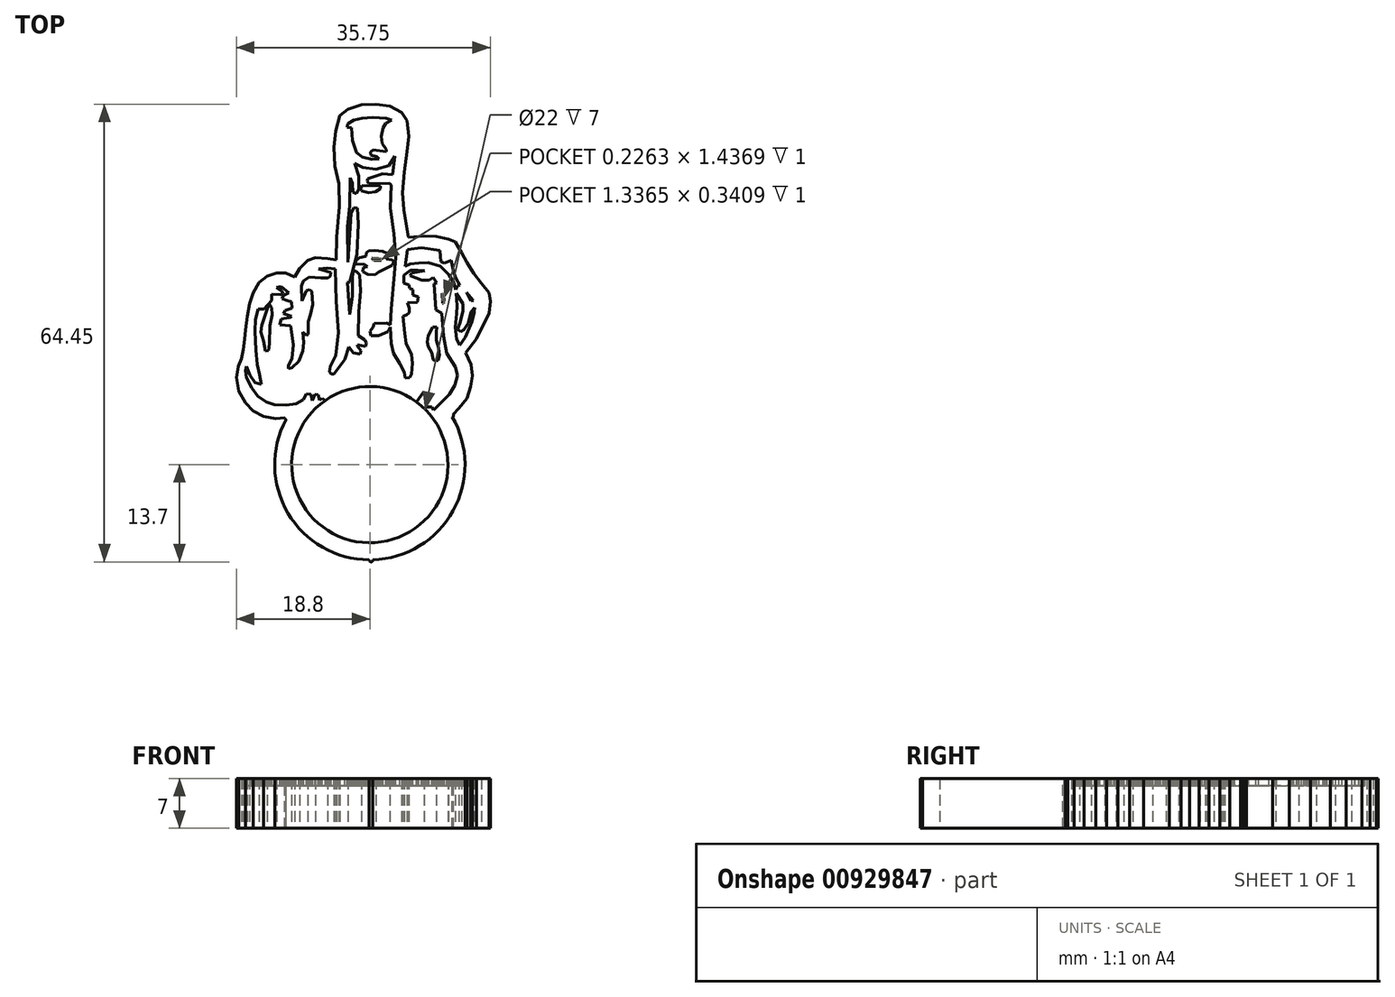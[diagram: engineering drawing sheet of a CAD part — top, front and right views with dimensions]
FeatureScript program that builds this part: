
annotation { "Feature Type Name" : "Feature", "Feature Type Description" : "" }
export const myFeature = defineFeature(function(context is Context, id is Id, definition is map)
    precondition{}
    {
        {
            var Q0;
            Q0=qCreatedBy(makeId("Top.planeOp"),FACE);
            var sketch = newSketch(context, id + "F0", { "sketchPlane" : qUnion([Q0])});
            skCircle(sketch, "E0", {"center": v(0, 0) * mm, "radius": 11 * mm});
            skCircle(sketch, "E1", {"center": v(0, 0) * mm, "radius": 13.4 * mm});
            skCircle(sketch, "E2", {"center": v(0, 0) * mm, "radius": 50.8 * mm, "construction": true});
            skLineSegment(sketch, "E3", {"start": v(0, 0) * mm, "end": v(-44, 25.4) * mm, "construction": true});
            skLineSegment(sketch, "E4", {"start": v(0, 0) * mm, "end": v(44, 25.4) * mm, "construction": true});
            skLineSegment(sketch, "E5", {"start": v(0, 0) * mm, "end": v(0, -50.8) * mm, "construction": true});
            skSolve(sketch);
        }
        {
            var Q0;
            Q0=qCreatedBy(makeId("Top.planeOp"),FACE);
            var sketch = newSketch(context, id + "F1", { "sketchPlane" : qUnion([Q0])});
            skCircle(sketch, "E6.0", {"center": v(0, 0) * mm, "radius": 13.4 * mm});
            skLineSegment(sketch, "E7", {"start": v(-11.66, 6.6) * mm, "end": v(-13.26, 6.5) * mm});
            skLineSegment(sketch, "E8", {"start": v(-13.26, 6.5) * mm, "end": v(-14.97, 6.82) * mm});
            skLineSegment(sketch, "E9", {"start": v(-14.97, 6.82) * mm, "end": v(-16.42, 7.53) * mm});
            skLineSegment(sketch, "E10", {"start": v(-16.42, 7.53) * mm, "end": v(-17.5, 8.7) * mm});
            skLineSegment(sketch, "E11", {"start": v(-17.5, 8.7) * mm, "end": v(-18.45, 10.38) * mm});
            skLineSegment(sketch, "E12", {"start": v(-18.45, 10.38) * mm, "end": v(-18.8, 12.26) * mm});
            skLineSegment(sketch, "E13", {"start": v(-18.8, 12.26) * mm, "end": v(-18.53, 13.84) * mm});
            skLineSegment(sketch, "E14", {"start": v(-18.53, 13.84) * mm, "end": v(-18.08, 14.9) * mm});
            skLineSegment(sketch, "E15", {"start": v(-18.08, 14.9) * mm, "end": v(-17.8, 16.19) * mm});
            skLineSegment(sketch, "E16", {"start": v(-17.8, 16.19) * mm, "end": v(-17.65, 17.63) * mm});
            skLineSegment(sketch, "E17", {"start": v(-17.65, 17.63) * mm, "end": v(-17.47, 19.02) * mm});
            skLineSegment(sketch, "E18", {"start": v(-17.47, 19.02) * mm, "end": v(-17.24, 20.92) * mm});
            skLineSegment(sketch, "E19", {"start": v(-17.24, 20.92) * mm, "end": v(-16.93, 22.67) * mm});
            skLineSegment(sketch, "E20", {"start": v(-16.93, 22.67) * mm, "end": v(-16.4, 24.2) * mm});
            skLineSegment(sketch, "E21", {"start": v(-16.4, 24.2) * mm, "end": v(-15.57, 25.63) * mm});
            skLineSegment(sketch, "E22", {"start": v(-15.57, 25.63) * mm, "end": v(-14.42, 26.52) * mm});
            skLineSegment(sketch, "E23", {"start": v(-14.42, 26.52) * mm, "end": v(-13.13, 26.99) * mm});
            skLineSegment(sketch, "E24", {"start": v(-13.13, 26.99) * mm, "end": v(-11.88, 26.99) * mm});
            skLineSegment(sketch, "E25", {"start": v(-11.88, 26.99) * mm, "end": v(-10.57, 26.44) * mm});
            skLineSegment(sketch, "E26", {"start": v(-10.57, 26.44) * mm, "end": v(-9.87, 27.6) * mm});
            skLineSegment(sketch, "E27", {"start": v(-9.87, 27.6) * mm, "end": v(-8.74, 28.74) * mm});
            skLineSegment(sketch, "E28", {"start": v(-8.74, 28.74) * mm, "end": v(-7.67, 29.15) * mm});
            skLineSegment(sketch, "E29", {"start": v(-7.67, 29.15) * mm, "end": v(-5.97, 29.04) * mm});
            skLineSegment(sketch, "E30", {"start": v(-5.97, 29.04) * mm, "end": v(-4.76, 28.84) * mm});
            skLineSegment(sketch, "E31", {"start": v(-4.76, 28.84) * mm, "end": v(-4.65, 32.06) * mm});
            skLineSegment(sketch, "E32", {"start": v(-4.65, 32.06) * mm, "end": v(-4.28, 36.3) * mm});
            skLineSegment(sketch, "E33", {"start": v(-4.28, 36.3) * mm, "end": v(-4.38, 39.56) * mm});
            skLineSegment(sketch, "E34", {"start": v(-4.38, 39.56) * mm, "end": v(-4.93, 42.06) * mm});
            skLineSegment(sketch, "E35", {"start": v(-4.93, 42.06) * mm, "end": v(-5.07, 44.68) * mm});
            skLineSegment(sketch, "E36", {"start": v(-5.07, 44.68) * mm, "end": v(-4.82, 46.97) * mm});
            skLineSegment(sketch, "E37", {"start": v(-4.82, 46.97) * mm, "end": v(-4.26, 49.12) * mm});
            skLineSegment(sketch, "E38", {"start": v(-4.26, 49.12) * mm, "end": v(-3.1, 50.06) * mm});
            skLineSegment(sketch, "E39", {"start": v(-3.1, 50.06) * mm, "end": v(-1.2, 50.67) * mm});
            skLineSegment(sketch, "E40", {"start": v(-1.2, 50.67) * mm, "end": v(0.84, 50.75) * mm});
            skLineSegment(sketch, "E41", {"start": v(0.84, 50.75) * mm, "end": v(2.84, 50.46) * mm});
            skLineSegment(sketch, "E42", {"start": v(2.84, 50.46) * mm, "end": v(4.45, 49.59) * mm});
            skLineSegment(sketch, "E43", {"start": v(4.45, 49.59) * mm, "end": v(5.24, 48.46) * mm});
            skLineSegment(sketch, "E44", {"start": v(5.24, 48.46) * mm, "end": v(5.47, 46.25) * mm});
            skLineSegment(sketch, "E45", {"start": v(5.47, 46.25) * mm, "end": v(5.24, 44.04) * mm});
            skLineSegment(sketch, "E46", {"start": v(5.24, 44.04) * mm, "end": v(4.88, 41.23) * mm});
            skLineSegment(sketch, "E47", {"start": v(4.88, 41.23) * mm, "end": v(4.6, 38.26) * mm});
            skLineSegment(sketch, "E48", {"start": v(4.6, 38.26) * mm, "end": v(4.78, 35.9) * mm});
            skLineSegment(sketch, "E49", {"start": v(4.78, 35.9) * mm, "end": v(5.44, 32.03) * mm});
            skLineSegment(sketch, "E50", {"start": v(5.44, 32.03) * mm, "end": v(7.63, 32.17) * mm});
            skLineSegment(sketch, "E51", {"start": v(7.63, 32.17) * mm, "end": v(9.34, 32.15) * mm});
            skLineSegment(sketch, "E52", {"start": v(9.34, 32.15) * mm, "end": v(11.1, 31.74) * mm});
            skLineSegment(sketch, "E53", {"start": v(11.1, 31.74) * mm, "end": v(12, 31.38) * mm});
            skLineSegment(sketch, "E54", {"start": v(12, 31.38) * mm, "end": v(12.92, 29.87) * mm});
            skLineSegment(sketch, "E55", {"start": v(12.92, 29.87) * mm, "end": v(13.67, 28.45) * mm});
            skLineSegment(sketch, "E56", {"start": v(13.67, 28.45) * mm, "end": v(14.6, 26.94) * mm});
            skLineSegment(sketch, "E57", {"start": v(14.6, 26.94) * mm, "end": v(15.74, 25.5) * mm});
            skLineSegment(sketch, "E58", {"start": v(15.74, 25.5) * mm, "end": v(16.8, 24.2) * mm});
            skLineSegment(sketch, "E59", {"start": v(16.8, 24.2) * mm, "end": v(16.95, 23.01) * mm});
            skLineSegment(sketch, "E60", {"start": v(16.95, 23.01) * mm, "end": v(16.77, 21.36) * mm});
            skLineSegment(sketch, "E61", {"start": v(16.77, 21.36) * mm, "end": v(14.99, 17.69) * mm});
            skLineSegment(sketch, "E62", {"start": v(14.99, 17.69) * mm, "end": v(13.47, 15.76) * mm});
            skLineSegment(sketch, "E63", {"start": v(13.47, 15.76) * mm, "end": v(14.26, 14.11) * mm});
            skLineSegment(sketch, "E64", {"start": v(14.26, 14.11) * mm, "end": v(14.47, 12.52) * mm});
            skLineSegment(sketch, "E65", {"start": v(14.47, 12.52) * mm, "end": v(14.2, 11.02) * mm});
            skLineSegment(sketch, "E66", {"start": v(14.2, 11.02) * mm, "end": v(13.68, 9.36) * mm});
            skLineSegment(sketch, "E67", {"start": v(13.68, 9.36) * mm, "end": v(12.54, 7.93) * mm});
            skLineSegment(sketch, "E68", {"start": v(12.54, 7.93) * mm, "end": v(11.5, 6.88) * mm});
            skSolve(sketch);
        }
        {
            var Q0;
            Q0=makeQuery(id+"F0.imprint","IMPRINT",FACE,{"disambiguationData":[TD([[makeQuery(id+"F0.imprint","IMPRINT",EDGE,{"derivedFrom":sQuery(id+"F0.wireOp",EDGE,"E0")}),-1.0]])]});
            extrude(context, id + "F2", {"entities" : qUnion([Q0]), "depth" : 7 * mm, "offsetDistance" : 25 * mm});
        }
        {
            var Q0;
            {var subQ0=sQuery(id+"F1.wireOp",EDGE,"E7");Q0=makeQuery(id+"F1.imprint","IMPRINT",FACE,{"disambiguationData":[TD([[makeQuery(id+"F1.imprint","IMPRINT",EDGE,{"derivedFrom":subQ0}),-1.0]])]});}
            extrude(context, id + "F3", {"entities" : qUnion([Q0]), "operationType" : NewBodyOperationType.ADD, "depth" : 7 * mm, "offsetDistance" : 25 * mm});
        }
        {
            var Q0;
            Q0=makeQuery(id+"F3.boolean.opBoolean","MERGE",FACE,{"derivedFrom":[makeQuery(id+"F2.opExtrude","CAP_FACE",FACE,{"disambiguationData":[OSD([sQuery(id+"F0.wireOp",EDGE,"E0"),sQuery(id+"F0.wireOp",EDGE,"E1")])],"isStart":false}),makeQuery(id+"F3.opExtrude","CAP_FACE",FACE,{"disambiguationData":[OSD([sQuery(id+"F1.wireOp",EDGE,"E6.0"),sQuery(id+"F1.wireOp",EDGE,"E7"),sQuery(id+"F1.wireOp",EDGE,"E8"),sQuery(id+"F1.wireOp",EDGE,"E9"),sQuery(id+"F1.wireOp",EDGE,"E10"),sQuery(id+"F1.wireOp",EDGE,"E11"),sQuery(id+"F1.wireOp",EDGE,"E12"),sQuery(id+"F1.wireOp",EDGE,"E13"),sQuery(id+"F1.wireOp",EDGE,"E14"),sQuery(id+"F1.wireOp",EDGE,"E15"),sQuery(id+"F1.wireOp",EDGE,"E16"),sQuery(id+"F1.wireOp",EDGE,"E17"),sQuery(id+"F1.wireOp",EDGE,"E18"),sQuery(id+"F1.wireOp",EDGE,"E19"),sQuery(id+"F1.wireOp",EDGE,"E20"),sQuery(id+"F1.wireOp",EDGE,"E21"),sQuery(id+"F1.wireOp",EDGE,"E22"),sQuery(id+"F1.wireOp",EDGE,"E23"),sQuery(id+"F1.wireOp",EDGE,"E24"),sQuery(id+"F1.wireOp",EDGE,"E25"),sQuery(id+"F1.wireOp",EDGE,"E26"),sQuery(id+"F1.wireOp",EDGE,"E27"),sQuery(id+"F1.wireOp",EDGE,"E28"),sQuery(id+"F1.wireOp",EDGE,"E29"),sQuery(id+"F1.wireOp",EDGE,"E30"),sQuery(id+"F1.wireOp",EDGE,"E31"),sQuery(id+"F1.wireOp",EDGE,"E32"),sQuery(id+"F1.wireOp",EDGE,"E33"),sQuery(id+"F1.wireOp",EDGE,"E34"),sQuery(id+"F1.wireOp",EDGE,"E35"),sQuery(id+"F1.wireOp",EDGE,"E36"),sQuery(id+"F1.wireOp",EDGE,"E37"),sQuery(id+"F1.wireOp",EDGE,"E38"),sQuery(id+"F1.wireOp",EDGE,"E39"),sQuery(id+"F1.wireOp",EDGE,"E40"),sQuery(id+"F1.wireOp",EDGE,"E41"),sQuery(id+"F1.wireOp",EDGE,"E42"),sQuery(id+"F1.wireOp",EDGE,"E43"),sQuery(id+"F1.wireOp",EDGE,"E44"),sQuery(id+"F1.wireOp",EDGE,"E45"),sQuery(id+"F1.wireOp",EDGE,"E46"),sQuery(id+"F1.wireOp",EDGE,"E47"),sQuery(id+"F1.wireOp",EDGE,"E48"),sQuery(id+"F1.wireOp",EDGE,"E49"),sQuery(id+"F1.wireOp",EDGE,"E50"),sQuery(id+"F1.wireOp",EDGE,"E51"),sQuery(id+"F1.wireOp",EDGE,"E52"),sQuery(id+"F1.wireOp",EDGE,"E53"),sQuery(id+"F1.wireOp",EDGE,"E54"),sQuery(id+"F1.wireOp",EDGE,"E55"),sQuery(id+"F1.wireOp",EDGE,"E56"),sQuery(id+"F1.wireOp",EDGE,"E57"),sQuery(id+"F1.wireOp",EDGE,"E58"),sQuery(id+"F1.wireOp",EDGE,"E59"),sQuery(id+"F1.wireOp",EDGE,"E60"),sQuery(id+"F1.wireOp",EDGE,"E61"),sQuery(id+"F1.wireOp",EDGE,"E62"),sQuery(id+"F1.wireOp",EDGE,"E63"),sQuery(id+"F1.wireOp",EDGE,"E64"),sQuery(id+"F1.wireOp",EDGE,"E65"),sQuery(id+"F1.wireOp",EDGE,"E66"),sQuery(id+"F1.wireOp",EDGE,"E67"),sQuery(id+"F1.wireOp",EDGE,"E68")])],"isStart":false})]});
            var sketch = newSketch(context, id + "F4", { "sketchPlane" : qUnion([Q0])});
            skLineSegment(sketch, "E69", {"start": v(-6.28, 9.03) * mm, "end": v(-6.73, 9.31) * mm});
            skLineSegment(sketch, "E70", {"start": v(-6.73, 9.31) * mm, "end": v(-7.11, 9.08) * mm});
            skLineSegment(sketch, "E71", {"start": v(-7.11, 9.08) * mm, "end": v(-7.3, 9.86) * mm});
            skLineSegment(sketch, "E72", {"start": v(-7.3, 9.86) * mm, "end": v(-7.74, 9.93) * mm});
            skLineSegment(sketch, "E73", {"start": v(-7.74, 9.93) * mm, "end": v(-8.13, 9) * mm});
            skLineSegment(sketch, "E74", {"start": v(-8.13, 9) * mm, "end": v(-8.32, 9.92) * mm});
            skLineSegment(sketch, "E75", {"start": v(-8.32, 9.92) * mm, "end": v(-8.93, 9.99) * mm});
            skLineSegment(sketch, "E76", {"start": v(-8.93, 9.99) * mm, "end": v(-9.4, 9.13) * mm});
            skLineSegment(sketch, "E77", {"start": v(-9.4, 9.13) * mm, "end": v(-10.37, 8.6) * mm});
            skLineSegment(sketch, "E78", {"start": v(-10.37, 8.6) * mm, "end": v(-11.8, 8.35) * mm});
            skLineSegment(sketch, "E79", {"start": v(-11.8, 8.35) * mm, "end": v(-13.42, 8.46) * mm});
            skLineSegment(sketch, "E80", {"start": v(-13.42, 8.46) * mm, "end": v(-14.6, 8.84) * mm});
            skLineSegment(sketch, "E81", {"start": v(-14.6, 8.84) * mm, "end": v(-15.77, 9.67) * mm});
            skLineSegment(sketch, "E82", {"start": v(-15.77, 9.67) * mm, "end": v(-16.6, 10.77) * mm});
            skLineSegment(sketch, "E83", {"start": v(-16.6, 10.77) * mm, "end": v(-17.36, 12.26) * mm});
            skLineSegment(sketch, "E84", {"start": v(-17.36, 12.26) * mm, "end": v(-17.52, 13.2) * mm});
            skLineSegment(sketch, "E85", {"start": v(-17.52, 13.2) * mm, "end": v(-17.37, 13.87) * mm});
            skLineSegment(sketch, "E86", {"start": v(-17.37, 13.87) * mm, "end": v(-16.84, 12.58) * mm});
            skLineSegment(sketch, "E87", {"start": v(-16.84, 12.58) * mm, "end": v(-16.14, 11.55) * mm});
            skLineSegment(sketch, "E88", {"start": v(-16.14, 11.55) * mm, "end": v(-15.3, 11.3) * mm});
            skLineSegment(sketch, "E89", {"start": v(-15.3, 11.3) * mm, "end": v(-15.55, 12.68) * mm});
            skLineSegment(sketch, "E90", {"start": v(-15.55, 12.68) * mm, "end": v(-15.87, 14.1) * mm});
            skLineSegment(sketch, "E91", {"start": v(-15.87, 14.1) * mm, "end": v(-16.07, 16.12) * mm});
            skLineSegment(sketch, "E92", {"start": v(-16.07, 16.12) * mm, "end": v(-16.2, 18.8) * mm});
            skLineSegment(sketch, "E93", {"start": v(-16.2, 18.8) * mm, "end": v(-16.1, 20.45) * mm});
            skLineSegment(sketch, "E94", {"start": v(-16.1, 20.45) * mm, "end": v(-15.74, 21.88) * mm});
            skLineSegment(sketch, "E95", {"start": v(-15.74, 21.88) * mm, "end": v(-14.91, 21.88) * mm});
            skLineSegment(sketch, "E96", {"start": v(-14.91, 21.88) * mm, "end": v(-13.81, 23.14) * mm});
            skLineSegment(sketch, "E97", {"start": v(-13.81, 23.14) * mm, "end": v(-13.8, 24.01) * mm});
            skLineSegment(sketch, "E98", {"start": v(-13.8, 24.01) * mm, "end": v(-12.59, 23.92) * mm});
            skLineSegment(sketch, "E99", {"start": v(-12.59, 23.92) * mm, "end": v(-12.22, 24.1) * mm});
            skLineSegment(sketch, "E100", {"start": v(-12.22, 24.1) * mm, "end": v(-12.41, 24.52) * mm});
            skLineSegment(sketch, "E101", {"start": v(-12.41, 24.52) * mm, "end": v(-13.13, 24.93) * mm});
            skLineSegment(sketch, "E102", {"start": v(-13.13, 24.93) * mm, "end": v(-12.47, 25.06) * mm});
            skLineSegment(sketch, "E103", {"start": v(-12.47, 25.06) * mm, "end": v(-11.38, 24.18) * mm});
            skLineSegment(sketch, "E104", {"start": v(-11.38, 24.18) * mm, "end": v(-12.17, 23.84) * mm});
            skLineSegment(sketch, "E105", {"start": v(-12.17, 23.84) * mm, "end": v(-12.37, 23.34) * mm});
            skLineSegment(sketch, "E106", {"start": v(-12.37, 23.34) * mm, "end": v(-11.69, 23.1) * mm});
            skLineSegment(sketch, "E107", {"start": v(-11.69, 23.1) * mm, "end": v(-11.03, 22.92) * mm});
            skLineSegment(sketch, "E108", {"start": v(-11.03, 22.92) * mm, "end": v(-10.93, 22.05) * mm});
            skLineSegment(sketch, "E109", {"start": v(-10.93, 22.05) * mm, "end": v(-11.92, 21.73) * mm});
            skLineSegment(sketch, "E110", {"start": v(-11.92, 21.73) * mm, "end": v(-12.18, 21.27) * mm});
            skLineSegment(sketch, "E111", {"start": v(-12.18, 21.27) * mm, "end": v(-11.03, 20.88) * mm});
            skLineSegment(sketch, "E112", {"start": v(-11.03, 20.88) * mm, "end": v(-11.37, 20.72) * mm});
            skLineSegment(sketch, "E113", {"start": v(-11.37, 20.72) * mm, "end": v(-12.51, 20.53) * mm});
            skLineSegment(sketch, "E114", {"start": v(-12.51, 20.53) * mm, "end": v(-12.66, 19.7) * mm});
            skLineSegment(sketch, "E115", {"start": v(-12.66, 19.7) * mm, "end": v(-11.12, 19.54) * mm});
            skLineSegment(sketch, "E116", {"start": v(-11.12, 19.54) * mm, "end": v(-10.78, 16.9) * mm});
            skLineSegment(sketch, "E117", {"start": v(-10.78, 16.9) * mm, "end": v(-10.96, 14.9) * mm});
            skLineSegment(sketch, "E118", {"start": v(-10.96, 14.9) * mm, "end": v(-11.48, 13.96) * mm});
            skLineSegment(sketch, "E119", {"start": v(-11.48, 13.96) * mm, "end": v(-11.47, 13.55) * mm});
            skLineSegment(sketch, "E120", {"start": v(-11.47, 13.55) * mm, "end": v(-10.97, 13.62) * mm});
            skLineSegment(sketch, "E121", {"start": v(-10.97, 13.62) * mm, "end": v(-10, 14.57) * mm});
            skLineSegment(sketch, "E122", {"start": v(-10, 14.57) * mm, "end": v(-9.44, 16.02) * mm});
            skLineSegment(sketch, "E123", {"start": v(-9.44, 16.02) * mm, "end": v(-9.3, 17.2) * mm});
            skLineSegment(sketch, "E124", {"start": v(-9.3, 17.2) * mm, "end": v(-9.46, 18.7) * mm});
            skLineSegment(sketch, "E125", {"start": v(-9.46, 18.7) * mm, "end": v(-8.96, 18.2) * mm});
            skLineSegment(sketch, "E126", {"start": v(-8.96, 18.2) * mm, "end": v(-8.66, 18.35) * mm});
            skLineSegment(sketch, "E127", {"start": v(-8.66, 18.35) * mm, "end": v(-8.68, 20.14) * mm});
            skLineSegment(sketch, "E128", {"start": v(-8.68, 20.14) * mm, "end": v(-8.36, 21.12) * mm});
            skLineSegment(sketch, "E129", {"start": v(-8.36, 21.12) * mm, "end": v(-8.04, 22.57) * mm});
            skLineSegment(sketch, "E130", {"start": v(-8.04, 22.57) * mm, "end": v(-8.17, 24.4) * mm});
            skLineSegment(sketch, "E131", {"start": v(-8.17, 24.4) * mm, "end": v(-8.47, 24.62) * mm});
            skLineSegment(sketch, "E132", {"start": v(-8.47, 24.62) * mm, "end": v(-8.93, 24.51) * mm});
            skLineSegment(sketch, "E133", {"start": v(-8.93, 24.51) * mm, "end": v(-9.55, 23.02) * mm});
            skLineSegment(sketch, "E134", {"start": v(-9.55, 23.02) * mm, "end": v(-9.62, 25.13) * mm});
            skLineSegment(sketch, "E135", {"start": v(-9.62, 25.13) * mm, "end": v(-9.36, 25.81) * mm});
            skLineSegment(sketch, "E136", {"start": v(-9.36, 25.81) * mm, "end": v(-8.56, 26.4) * mm});
            skLineSegment(sketch, "E137", {"start": v(-8.56, 26.4) * mm, "end": v(-6.87, 26.32) * mm});
            skLineSegment(sketch, "E138", {"start": v(-6.87, 26.32) * mm, "end": v(-5.9, 26.28) * mm});
            skLineSegment(sketch, "E139", {"start": v(-5.9, 26.28) * mm, "end": v(-5.56, 26.56) * mm});
            skLineSegment(sketch, "E140", {"start": v(-5.56, 26.56) * mm, "end": v(-5.52, 27.04) * mm});
            skLineSegment(sketch, "E141", {"start": v(-5.52, 27.04) * mm, "end": v(-7.22, 27.53) * mm});
            skLineSegment(sketch, "E142", {"start": v(-7.22, 27.53) * mm, "end": v(-6, 27.66) * mm});
            skLineSegment(sketch, "E143", {"start": v(-6, 27.66) * mm, "end": v(-4.84, 27.55) * mm});
            skLineSegment(sketch, "E144", {"start": v(-4.84, 27.55) * mm, "end": v(-4.73, 23) * mm});
            skLineSegment(sketch, "E145", {"start": v(-4.73, 23) * mm, "end": v(-4.43, 18.61) * mm});
            skLineSegment(sketch, "E146", {"start": v(-4.43, 18.61) * mm, "end": v(-4.83, 15.4) * mm});
            skLineSegment(sketch, "E147", {"start": v(-4.83, 15.4) * mm, "end": v(-5.53, 13.85) * mm});
            skLineSegment(sketch, "E148", {"start": v(-5.53, 13.85) * mm, "end": v(-5.7, 13.08) * mm});
            skLineSegment(sketch, "E149", {"start": v(-5.7, 13.08) * mm, "end": v(-5.44, 12.76) * mm});
            skLineSegment(sketch, "E150", {"start": v(-5.44, 12.76) * mm, "end": v(-5.09, 12.77) * mm});
            skLineSegment(sketch, "E151", {"start": v(-5.09, 12.77) * mm, "end": v(-3.56, 14.79) * mm});
            skLineSegment(sketch, "E152", {"start": v(-3.56, 14.79) * mm, "end": v(-2.94, 16.55) * mm});
            skLineSegment(sketch, "E153", {"start": v(-2.94, 16.55) * mm, "end": v(-2.35, 15.78) * mm});
            skLineSegment(sketch, "E154", {"start": v(-2.35, 15.78) * mm, "end": v(-1.34, 15.59) * mm});
            skLineSegment(sketch, "E155", {"start": v(-1.34, 15.59) * mm, "end": v(-1.24, 16.08) * mm});
            skLineSegment(sketch, "E156", {"start": v(-1.24, 16.08) * mm, "end": v(-1.7, 16.55) * mm});
            skLineSegment(sketch, "E157", {"start": v(-1.7, 16.55) * mm, "end": v(-1.78, 16.88) * mm});
            skLineSegment(sketch, "E158", {"start": v(-1.78, 16.88) * mm, "end": v(-0.6, 16.65) * mm});
            skLineSegment(sketch, "E159", {"start": v(-0.6, 16.65) * mm, "end": v(-0.48, 17.12) * mm});
            skLineSegment(sketch, "E160", {"start": v(-0.48, 17.12) * mm, "end": v(-0.72, 17.56) * mm});
            skLineSegment(sketch, "E161", {"start": v(-0.72, 17.56) * mm, "end": v(-1.65, 18.16) * mm});
            skLineSegment(sketch, "E162", {"start": v(-1.65, 18.16) * mm, "end": v(-1.58, 21.5) * mm});
            skLineSegment(sketch, "E163", {"start": v(-1.58, 21.5) * mm, "end": v(-1.33, 24.47) * mm});
            skLineSegment(sketch, "E164", {"start": v(-1.33, 24.47) * mm, "end": v(-1.46, 26.71) * mm});
            skLineSegment(sketch, "E165", {"start": v(-1.46, 26.71) * mm, "end": v(-1.97, 27.24) * mm});
            skLineSegment(sketch, "E166", {"start": v(-1.97, 27.24) * mm, "end": v(-2.31, 27.21) * mm});
            skLineSegment(sketch, "E167", {"start": v(-2.31, 27.21) * mm, "end": v(-2.43, 26.57) * mm});
            skLineSegment(sketch, "E168", {"start": v(-2.43, 26.57) * mm, "end": v(-2.44, 23.76) * mm});
            skLineSegment(sketch, "E169", {"start": v(-2.44, 23.76) * mm, "end": v(-2.81, 21.13) * mm});
            skLineSegment(sketch, "E170", {"start": v(-2.81, 21.13) * mm, "end": v(-3.18, 25.64) * mm});
            skLineSegment(sketch, "E171", {"start": v(-3.18, 25.64) * mm, "end": v(-2.84, 25.7) * mm});
            skLineSegment(sketch, "E172", {"start": v(-2.84, 25.7) * mm, "end": v(-1.83, 29.61) * mm});
            skLineSegment(sketch, "E173", {"start": v(-1.83, 29.61) * mm, "end": v(-1.62, 33.92) * mm});
            skLineSegment(sketch, "E174", {"start": v(-1.62, 33.92) * mm, "end": v(-1.73, 36.16) * mm});
            skLineSegment(sketch, "E175", {"start": v(-1.73, 36.16) * mm, "end": v(-2.24, 36.2) * mm});
            skLineSegment(sketch, "E176", {"start": v(-2.24, 36.2) * mm, "end": v(-2.64, 35.35) * mm});
            skLineSegment(sketch, "E177", {"start": v(-2.64, 35.35) * mm, "end": v(-3.08, 28.52) * mm});
            skLineSegment(sketch, "E178", {"start": v(-3.08, 28.52) * mm, "end": v(-3.15, 33.53) * mm});
            skLineSegment(sketch, "E179", {"start": v(-3.15, 33.53) * mm, "end": v(-2.86, 36.43) * mm});
            skLineSegment(sketch, "E180", {"start": v(-2.86, 36.43) * mm, "end": v(-2.75, 40.4) * mm});
            skLineSegment(sketch, "E181", {"start": v(-2.75, 40.4) * mm, "end": v(-2.47, 39.64) * mm});
            skLineSegment(sketch, "E182", {"start": v(-2.47, 39.64) * mm, "end": v(-2.37, 38.33) * mm});
            skLineSegment(sketch, "E183", {"start": v(-2.37, 38.33) * mm, "end": v(-1.9, 38.19) * mm});
            skLineSegment(sketch, "E184", {"start": v(-1.9, 38.19) * mm, "end": v(-1.53, 38.77) * mm});
            skLineSegment(sketch, "E185", {"start": v(-1.53, 38.77) * mm, "end": v(-1.58, 40.62) * mm});
            skLineSegment(sketch, "E186", {"start": v(-1.58, 40.62) * mm, "end": v(-2.14, 42.43) * mm});
            skLineSegment(sketch, "E187", {"start": v(-2.14, 42.43) * mm, "end": v(-0.98, 41.84) * mm});
            skLineSegment(sketch, "E188", {"start": v(-0.98, 41.84) * mm, "end": v(0.88, 41.62) * mm});
            skLineSegment(sketch, "E189", {"start": v(0.88, 41.62) * mm, "end": v(2.72, 42.1) * mm});
            skLineSegment(sketch, "E190", {"start": v(2.72, 42.1) * mm, "end": v(3.53, 43.4) * mm});
            skLineSegment(sketch, "E191", {"start": v(3.53, 43.4) * mm, "end": v(3.2, 40.8) * mm});
            skLineSegment(sketch, "E192", {"start": v(3.2, 40.8) * mm, "end": v(1.83, 40.95) * mm});
            skLineSegment(sketch, "E193", {"start": v(1.83, 40.95) * mm, "end": v(-0.27, 40.28) * mm});
            skLineSegment(sketch, "E194", {"start": v(-0.27, 40.28) * mm, "end": v(-0.36, 39.92) * mm});
            skLineSegment(sketch, "E195", {"start": v(-0.36, 39.92) * mm, "end": v(-0.14, 39.59) * mm});
            skLineSegment(sketch, "E196", {"start": v(-0.14, 39.59) * mm, "end": v(2.77, 39.65) * mm});
            skLineSegment(sketch, "E197", {"start": v(2.77, 39.65) * mm, "end": v(2.99, 39.34) * mm});
            skLineSegment(sketch, "E198", {"start": v(2.99, 39.34) * mm, "end": v(2.86, 36.15) * mm});
            skLineSegment(sketch, "E199", {"start": v(2.86, 36.15) * mm, "end": v(3.4, 32.53) * mm});
            skLineSegment(sketch, "E200", {"start": v(3.4, 32.53) * mm, "end": v(3.63, 29.2) * mm});
            skLineSegment(sketch, "E201", {"start": v(3.63, 29.2) * mm, "end": v(3.43, 26.86) * mm});
            skLineSegment(sketch, "E202", {"start": v(3.43, 26.86) * mm, "end": v(3.02, 21.89) * mm});
            skLineSegment(sketch, "E203", {"start": v(3.02, 21.89) * mm, "end": v(2.9, 19.7) * mm});
            skLineSegment(sketch, "E204", {"start": v(2.9, 19.7) * mm, "end": v(2.4, 19.93) * mm});
            skLineSegment(sketch, "E205", {"start": v(2.4, 19.93) * mm, "end": v(0.59, 19.9) * mm});
            skLineSegment(sketch, "E206", {"start": v(0.59, 19.9) * mm, "end": v(0.48, 19.34) * mm});
            skLineSegment(sketch, "E207", {"start": v(0.48, 19.34) * mm, "end": v(0.02, 18.76) * mm});
            skLineSegment(sketch, "E208", {"start": v(0.02, 18.76) * mm, "end": v(0.15, 18.13) * mm});
            skLineSegment(sketch, "E209", {"start": v(0.15, 18.13) * mm, "end": v(1.23, 18.18) * mm});
            skLineSegment(sketch, "E210", {"start": v(1.23, 18.18) * mm, "end": v(2.55, 18.74) * mm});
            skLineSegment(sketch, "E211", {"start": v(2.55, 18.74) * mm, "end": v(2.88, 19.38) * mm});
            skLineSegment(sketch, "E212", {"start": v(2.88, 19.38) * mm, "end": v(3, 17.1) * mm});
            skLineSegment(sketch, "E213", {"start": v(3, 17.1) * mm, "end": v(3.35, 15.7) * mm});
            skLineSegment(sketch, "E214", {"start": v(3.35, 15.7) * mm, "end": v(4.21, 14.2) * mm});
            skLineSegment(sketch, "E215", {"start": v(4.21, 14.2) * mm, "end": v(4.84, 13.03) * mm});
            skLineSegment(sketch, "E216", {"start": v(4.84, 13.03) * mm, "end": v(5, 12.2) * mm});
            skLineSegment(sketch, "E217", {"start": v(5, 12.2) * mm, "end": v(5.58, 12.25) * mm});
            skLineSegment(sketch, "E218", {"start": v(5.58, 12.25) * mm, "end": v(5.86, 12.8) * mm});
            skLineSegment(sketch, "E219", {"start": v(5.86, 12.8) * mm, "end": v(6, 14.3) * mm});
            skLineSegment(sketch, "E220", {"start": v(6, 14.3) * mm, "end": v(5.85, 15.48) * mm});
            skLineSegment(sketch, "E221", {"start": v(5.85, 15.48) * mm, "end": v(5.09, 17.06) * mm});
            skLineSegment(sketch, "E222", {"start": v(5.09, 17.06) * mm, "end": v(4.92, 18.5) * mm});
            skLineSegment(sketch, "E223", {"start": v(4.92, 18.5) * mm, "end": v(4.63, 20.88) * mm});
            skLineSegment(sketch, "E224", {"start": v(4.63, 20.88) * mm, "end": v(5.2, 21.1) * mm});
            skLineSegment(sketch, "E225", {"start": v(5.2, 21.1) * mm, "end": v(5.53, 21.39) * mm});
            skLineSegment(sketch, "E226", {"start": v(5.53, 21.39) * mm, "end": v(5.55, 22.03) * mm});
            skLineSegment(sketch, "E227", {"start": v(5.55, 22.03) * mm, "end": v(5.28, 22.77) * mm});
            skLineSegment(sketch, "E228", {"start": v(5.28, 22.77) * mm, "end": v(6.7, 22.86) * mm});
            skLineSegment(sketch, "E229", {"start": v(6.7, 22.86) * mm, "end": v(6.8, 23.64) * mm});
            skLineSegment(sketch, "E230", {"start": v(6.8, 23.64) * mm, "end": v(6.05, 23.85) * mm});
            skLineSegment(sketch, "E231", {"start": v(6.05, 23.85) * mm, "end": v(6.08, 24.66) * mm});
            skLineSegment(sketch, "E232", {"start": v(6.08, 24.66) * mm, "end": v(5.58, 24.83) * mm});
            skLineSegment(sketch, "E233", {"start": v(5.58, 24.83) * mm, "end": v(5.47, 25.37) * mm});
            skLineSegment(sketch, "E234", {"start": v(5.47, 25.37) * mm, "end": v(4.78, 25.5) * mm});
            skLineSegment(sketch, "E235", {"start": v(4.78, 25.5) * mm, "end": v(4.8, 26.65) * mm});
            skLineSegment(sketch, "E236", {"start": v(4.8, 26.65) * mm, "end": v(5.84, 27.41) * mm});
            skLineSegment(sketch, "E237", {"start": v(5.84, 27.41) * mm, "end": v(7.73, 27.3) * mm});
            skLineSegment(sketch, "E238", {"start": v(7.73, 27.3) * mm, "end": v(5.89, 27) * mm});
            skLineSegment(sketch, "E239", {"start": v(5.89, 27) * mm, "end": v(5.7, 26.63) * mm});
            skLineSegment(sketch, "E240", {"start": v(5.7, 26.63) * mm, "end": v(7.3, 25.97) * mm});
            skLineSegment(sketch, "E241", {"start": v(7.3, 25.97) * mm, "end": v(8.34, 25.94) * mm});
            skLineSegment(sketch, "E242", {"start": v(8.34, 25.94) * mm, "end": v(8.9, 26.33) * mm});
            skLineSegment(sketch, "E243", {"start": v(8.9, 26.33) * mm, "end": v(9.42, 25.6) * mm});
            skLineSegment(sketch, "E244", {"start": v(9.42, 25.6) * mm, "end": v(9.05, 25.48) * mm});
            skLineSegment(sketch, "E245", {"start": v(9.05, 25.48) * mm, "end": v(9.3, 21.78) * mm});
            skLineSegment(sketch, "E246", {"start": v(9.3, 21.78) * mm, "end": v(10.11, 21.36) * mm});
            skLineSegment(sketch, "E247", {"start": v(10.11, 21.36) * mm, "end": v(10.36, 18.08) * mm});
            skLineSegment(sketch, "E248", {"start": v(10.36, 18.08) * mm, "end": v(10.84, 15.68) * mm});
            skLineSegment(sketch, "E249", {"start": v(10.84, 15.68) * mm, "end": v(12.05, 13.77) * mm});
            skLineSegment(sketch, "E250", {"start": v(12.05, 13.77) * mm, "end": v(12.32, 12.56) * mm});
            skLineSegment(sketch, "E251", {"start": v(12.32, 12.56) * mm, "end": v(11.96, 11.15) * mm});
            skLineSegment(sketch, "E252", {"start": v(11.96, 11.15) * mm, "end": v(11.18, 9.9) * mm});
            skLineSegment(sketch, "E253", {"start": v(11.18, 9.9) * mm, "end": v(8.95, 7.7) * mm});
            skLineSegment(sketch, "E254", {"start": v(8.95, 7.7) * mm, "end": v(8.73, 8.1) * mm});
            skLineSegment(sketch, "E255", {"start": v(8.73, 8.1) * mm, "end": v(7.96, 8.13) * mm});
            skLineSegment(sketch, "E256", {"start": v(7.96, 8.13) * mm, "end": v(8.1, 10.06) * mm});
            skLineSegment(sketch, "E257", {"start": v(8.1, 10.06) * mm, "end": v(7.49, 10.15) * mm});
            skLineSegment(sketch, "E258", {"start": v(7.49, 10.15) * mm, "end": v(6.52, 8.8) * mm});
            skLineSegment(sketch, "E259", {"start": v(-3.24, 47.52) * mm, "end": v(-2.6, 47.44) * mm});
            skLineSegment(sketch, "E260", {"start": v(-2.6, 47.44) * mm, "end": v(-2.46, 45.64) * mm});
            skLineSegment(sketch, "E261", {"start": v(-2.46, 45.64) * mm, "end": v(-1.86, 43.96) * mm});
            skLineSegment(sketch, "E262", {"start": v(-1.86, 43.96) * mm, "end": v(-1.08, 43.34) * mm});
            skLineSegment(sketch, "E263", {"start": v(-1.08, 43.34) * mm, "end": v(0.29, 43) * mm});
            skLineSegment(sketch, "E264", {"start": v(0.29, 43) * mm, "end": v(1.32, 43.07) * mm});
            skLineSegment(sketch, "E265", {"start": v(1.32, 43.07) * mm, "end": v(0.97, 43.38) * mm});
            skLineSegment(sketch, "E266", {"start": v(0.97, 43.38) * mm, "end": v(0.14, 43.6) * mm});
            skLineSegment(sketch, "E267", {"start": v(0.14, 43.6) * mm, "end": v(0.08, 44.02) * mm});
            skLineSegment(sketch, "E268", {"start": v(0.08, 44.02) * mm, "end": v(0.5, 44.34) * mm});
            skLineSegment(sketch, "E269", {"start": v(0.5, 44.34) * mm, "end": v(2.29, 44.07) * mm});
            skLineSegment(sketch, "E270", {"start": v(2.29, 44.07) * mm, "end": v(2.29, 44.42) * mm});
            skLineSegment(sketch, "E271", {"start": v(2.29, 44.42) * mm, "end": v(1.76, 45.2) * mm});
            skLineSegment(sketch, "E272", {"start": v(1.76, 45.2) * mm, "end": v(1.63, 46.25) * mm});
            skLineSegment(sketch, "E273", {"start": v(1.63, 46.25) * mm, "end": v(1.87, 47.45) * mm});
            skLineSegment(sketch, "E274", {"start": v(1.87, 47.45) * mm, "end": v(2.27, 48.08) * mm});
            skLineSegment(sketch, "E275", {"start": v(2.27, 48.08) * mm, "end": v(3.07, 48.49) * mm});
            skLineSegment(sketch, "E276", {"start": v(3.07, 48.49) * mm, "end": v(2.3, 48.75) * mm});
            skLineSegment(sketch, "E277", {"start": v(2.3, 48.75) * mm, "end": v(0.39, 48.9) * mm});
            skLineSegment(sketch, "E278", {"start": v(0.39, 48.9) * mm, "end": v(-1.13, 48.78) * mm});
            skLineSegment(sketch, "E279", {"start": v(-1.13, 48.78) * mm, "end": v(-2.24, 48.53) * mm});
            skLineSegment(sketch, "E280", {"start": v(-2.24, 48.53) * mm, "end": v(-3.09, 48.03) * mm});
            skLineSegment(sketch, "E281", {"start": v(-3.09, 48.03) * mm, "end": v(-3.24, 47.52) * mm});
            skLineSegment(sketch, "E282", {"start": v(-1.14, 39.29) * mm, "end": v(-1.3, 38.77) * mm});
            skLineSegment(sketch, "E283", {"start": v(-1.3, 38.77) * mm, "end": v(-1.18, 38.55) * mm});
            skLineSegment(sketch, "E284", {"start": v(-1.18, 38.55) * mm, "end": v(-0.14, 38.28) * mm});
            skLineSegment(sketch, "E285", {"start": v(-0.14, 38.28) * mm, "end": v(0.8, 38.4) * mm});
            skLineSegment(sketch, "E286", {"start": v(0.8, 38.4) * mm, "end": v(1.51, 38.86) * mm});
            skLineSegment(sketch, "E287", {"start": v(1.51, 38.86) * mm, "end": v(1.48, 39.26) * mm});
            skLineSegment(sketch, "E288", {"start": v(1.48, 39.26) * mm, "end": v(-1.14, 39.29) * mm});
            skLineSegment(sketch, "E289", {"start": v(0.3, 29.1) * mm, "end": v(0.62, 28.8) * mm});
            skLineSegment(sketch, "E290", {"start": v(0.62, 28.8) * mm, "end": v(1.63, 28.75) * mm});
            skLineSegment(sketch, "E291", {"start": v(1.63, 28.75) * mm, "end": v(1.16, 29.04) * mm});
            skLineSegment(sketch, "E292", {"start": v(1.16, 29.04) * mm, "end": v(0.3, 29.1) * mm});
            skLineSegment(sketch, "E293", {"start": v(-0.56, 29.33) * mm, "end": v(-1.4, 29.12) * mm});
            skLineSegment(sketch, "E294", {"start": v(-1.4, 29.12) * mm, "end": v(-1.93, 28.74) * mm});
            skLineSegment(sketch, "E295", {"start": v(-1.93, 28.74) * mm, "end": v(-1.98, 28.23) * mm});
            skLineSegment(sketch, "E296", {"start": v(-1.98, 28.23) * mm, "end": v(-0.76, 28.22) * mm});
            skLineSegment(sketch, "E297", {"start": v(-0.76, 28.22) * mm, "end": v(-0.36, 27.9) * mm});
            skLineSegment(sketch, "E298", {"start": v(-0.36, 27.9) * mm, "end": v(-0.92, 27.77) * mm});
            skLineSegment(sketch, "E299", {"start": v(-0.92, 27.77) * mm, "end": v(-0.99, 27.15) * mm});
            skLineSegment(sketch, "E300", {"start": v(-0.99, 27.15) * mm, "end": v(-0.3, 26.8) * mm});
            skLineSegment(sketch, "E301", {"start": v(-0.3, 26.8) * mm, "end": v(0.71, 26.75) * mm});
            skLineSegment(sketch, "E302", {"start": v(0.71, 26.75) * mm, "end": v(1.23, 27.1) * mm});
            skLineSegment(sketch, "E303", {"start": v(1.23, 27.1) * mm, "end": v(3.15, 28.08) * mm});
            skLineSegment(sketch, "E304", {"start": v(3.15, 28.08) * mm, "end": v(3.4, 28.53) * mm});
            skLineSegment(sketch, "E305", {"start": v(3.4, 28.53) * mm, "end": v(3.14, 28.82) * mm});
            skLineSegment(sketch, "E306", {"start": v(3.14, 28.82) * mm, "end": v(2.3, 28.98) * mm});
            skLineSegment(sketch, "E307", {"start": v(2.3, 28.98) * mm, "end": v(2.4, 29.8) * mm});
            skLineSegment(sketch, "E308", {"start": v(2.4, 29.8) * mm, "end": v(1.8, 30.06) * mm});
            skLineSegment(sketch, "E309", {"start": v(1.8, 30.06) * mm, "end": v(0.64, 30.16) * mm});
            skLineSegment(sketch, "E310", {"start": v(0.64, 30.16) * mm, "end": v(-0.15, 30.07) * mm});
            skLineSegment(sketch, "E311", {"start": v(-0.15, 30.07) * mm, "end": v(-0.47, 29.82) * mm});
            skLineSegment(sketch, "E312", {"start": v(-0.47, 29.82) * mm, "end": v(-0.56, 29.33) * mm});
            skLineSegment(sketch, "E313", {"start": v(-14.73, 16.01) * mm, "end": v(-14.27, 16.03) * mm});
            skLineSegment(sketch, "E314", {"start": v(-14.27, 16.03) * mm, "end": v(-14.16, 17.05) * mm});
            skLineSegment(sketch, "E315", {"start": v(-14.16, 17.05) * mm, "end": v(-14.09, 19.59) * mm});
            skLineSegment(sketch, "E316", {"start": v(-14.09, 19.59) * mm, "end": v(-13.79, 21.1) * mm});
            skLineSegment(sketch, "E317", {"start": v(-13.79, 21.1) * mm, "end": v(-13.82, 22.13) * mm});
            skLineSegment(sketch, "E318", {"start": v(-13.82, 22.13) * mm, "end": v(-14.1, 22.46) * mm});
            skLineSegment(sketch, "E319", {"start": v(-14.1, 22.46) * mm, "end": v(-14.3, 22.42) * mm});
            skLineSegment(sketch, "E320", {"start": v(-14.3, 22.42) * mm, "end": v(-14.59, 21.52) * mm});
            skLineSegment(sketch, "E321", {"start": v(-14.59, 21.52) * mm, "end": v(-15.2, 19.62) * mm});
            skLineSegment(sketch, "E322", {"start": v(-15.2, 19.62) * mm, "end": v(-15.34, 18.67) * mm});
            skLineSegment(sketch, "E323", {"start": v(-15.34, 18.67) * mm, "end": v(-14.99, 17.4) * mm});
            skLineSegment(sketch, "E324", {"start": v(-14.99, 17.4) * mm, "end": v(-14.73, 16.01) * mm});
            skLineSegment(sketch, "E325", {"start": v(8.93, 14.8) * mm, "end": v(8.72, 15.73) * mm});
            skLineSegment(sketch, "E326", {"start": v(8.72, 15.73) * mm, "end": v(8.19, 16.65) * mm});
            skLineSegment(sketch, "E327", {"start": v(8.19, 16.65) * mm, "end": v(8.08, 17.3) * mm});
            skLineSegment(sketch, "E328", {"start": v(8.08, 17.3) * mm, "end": v(8.22, 18.2) * mm});
            skLineSegment(sketch, "E329", {"start": v(8.22, 18.2) * mm, "end": v(8.87, 19.4) * mm});
            skLineSegment(sketch, "E330", {"start": v(8.87, 19.4) * mm, "end": v(9.43, 19.4) * mm});
            skLineSegment(sketch, "E331", {"start": v(9.43, 19.4) * mm, "end": v(9.34, 18.68) * mm});
            skLineSegment(sketch, "E332", {"start": v(9.34, 18.68) * mm, "end": v(9.34, 17.54) * mm});
            skLineSegment(sketch, "E333", {"start": v(9.34, 17.54) * mm, "end": v(9.69, 16.46) * mm});
            skLineSegment(sketch, "E334", {"start": v(9.69, 16.46) * mm, "end": v(9.77, 15.44) * mm});
            skLineSegment(sketch, "E335", {"start": v(9.77, 15.44) * mm, "end": v(9.6, 14.67) * mm});
            skLineSegment(sketch, "E336", {"start": v(9.6, 14.67) * mm, "end": v(9.17, 14.62) * mm});
            skLineSegment(sketch, "E337", {"start": v(9.17, 14.62) * mm, "end": v(8.93, 14.8) * mm});
            skLineSegment(sketch, "E338", {"start": v(4.95, 27.96) * mm, "end": v(5.28, 30.3) * mm});
            skLineSegment(sketch, "E339", {"start": v(5.28, 30.3) * mm, "end": v(7.29, 30.55) * mm});
            skLineSegment(sketch, "E340", {"start": v(7.29, 30.55) * mm, "end": v(9.85, 30.16) * mm});
            skLineSegment(sketch, "E341", {"start": v(9.85, 30.16) * mm, "end": v(9.97, 28.6) * mm});
            skLineSegment(sketch, "E342", {"start": v(9.97, 28.6) * mm, "end": v(10.52, 28.4) * mm});
            skLineSegment(sketch, "E343", {"start": v(10.52, 28.4) * mm, "end": v(11.43, 28.74) * mm});
            skLineSegment(sketch, "E344", {"start": v(11.43, 28.74) * mm, "end": v(11.7, 27.48) * mm});
            skLineSegment(sketch, "E345", {"start": v(11.7, 27.48) * mm, "end": v(12.1, 26.27) * mm});
            skLineSegment(sketch, "E346", {"start": v(12.1, 26.27) * mm, "end": v(12.69, 25.3) * mm});
            skLineSegment(sketch, "E347", {"start": v(12.69, 25.3) * mm, "end": v(12.31, 25.2) * mm});
            skLineSegment(sketch, "E348", {"start": v(12.31, 25.2) * mm, "end": v(12.08, 24.63) * mm});
            skLineSegment(sketch, "E349", {"start": v(12.08, 24.63) * mm, "end": v(11.83, 25.58) * mm});
            skLineSegment(sketch, "E350", {"start": v(11.83, 25.58) * mm, "end": v(11.16, 26.73) * mm});
            skLineSegment(sketch, "E351", {"start": v(11.16, 26.73) * mm, "end": v(9.95, 27.9) * mm});
            skLineSegment(sketch, "E352", {"start": v(9.95, 27.9) * mm, "end": v(8.19, 28.44) * mm});
            skLineSegment(sketch, "E353", {"start": v(8.19, 28.44) * mm, "end": v(6.88, 28.4) * mm});
            skLineSegment(sketch, "E354", {"start": v(6.88, 28.4) * mm, "end": v(5.67, 28.29) * mm});
            skLineSegment(sketch, "E355", {"start": v(5.67, 28.29) * mm, "end": v(4.95, 27.96) * mm});
            skLineSegment(sketch, "E356", {"start": v(12.17, 24.1) * mm, "end": v(12.3, 22.38) * mm});
            skLineSegment(sketch, "E357", {"start": v(12.3, 22.38) * mm, "end": v(12.2, 21.25) * mm});
            skLineSegment(sketch, "E358", {"start": v(12.2, 21.25) * mm, "end": v(12.04, 19.38) * mm});
            skLineSegment(sketch, "E359", {"start": v(12.04, 19.38) * mm, "end": v(12.22, 17.66) * mm});
            skLineSegment(sketch, "E360", {"start": v(12.22, 17.66) * mm, "end": v(12.64, 16.83) * mm});
            skLineSegment(sketch, "E361", {"start": v(12.64, 16.83) * mm, "end": v(13.44, 17.89) * mm});
            skLineSegment(sketch, "E362", {"start": v(13.44, 17.89) * mm, "end": v(14.35, 20.15) * mm});
            skLineSegment(sketch, "E363", {"start": v(14.35, 20.15) * mm, "end": v(14.73, 21.46) * mm});
            skLineSegment(sketch, "E364", {"start": v(14.73, 21.46) * mm, "end": v(14.77, 22.13) * mm});
            skLineSegment(sketch, "E365", {"start": v(14.77, 22.13) * mm, "end": v(14.24, 21.5) * mm});
            skLineSegment(sketch, "E366", {"start": v(14.24, 21.5) * mm, "end": v(13.84, 19.96) * mm});
            skLineSegment(sketch, "E367", {"start": v(13.84, 19.96) * mm, "end": v(13.23, 18.96) * mm});
            skLineSegment(sketch, "E368", {"start": v(13.23, 18.96) * mm, "end": v(12.76, 18.76) * mm});
            skLineSegment(sketch, "E369", {"start": v(12.76, 18.76) * mm, "end": v(12.34, 19.02) * mm});
            skLineSegment(sketch, "E370", {"start": v(12.34, 19.02) * mm, "end": v(12.69, 19.9) * mm});
            skLineSegment(sketch, "E371", {"start": v(12.69, 19.9) * mm, "end": v(13.08, 21.57) * mm});
            skLineSegment(sketch, "E372", {"start": v(13.08, 21.57) * mm, "end": v(13.1, 22.67) * mm});
            skLineSegment(sketch, "E373", {"start": v(13.1, 22.67) * mm, "end": v(12.17, 24.1) * mm});
            skLineSegment(sketch, "E374", {"start": v(13.58, 24.26) * mm, "end": v(14.28, 23.06) * mm});
            skLineSegment(sketch, "E375", {"start": v(14.28, 23.06) * mm, "end": v(14.6, 23.1) * mm});
            skLineSegment(sketch, "E376", {"start": v(14.6, 23.1) * mm, "end": v(13.58, 24.26) * mm});
            skLineSegment(sketch, "E377", {"start": v(10.23, 22.73) * mm, "end": v(10.21, 24.14) * mm});
            skLineSegment(sketch, "E378", {"start": v(10.21, 24.14) * mm, "end": v(10.44, 23.31) * mm});
            skLineSegment(sketch, "E379", {"start": v(10.44, 23.31) * mm, "end": v(10.38, 22.7) * mm});
            skLineSegment(sketch, "E380", {"start": v(10.38, 22.7) * mm, "end": v(10.23, 22.73) * mm});
            skSolve(sketch);
        }
        {
            var Q0;
            {var subQ4=sQuery(id+"F4.wireOp",EDGE,"E69");Q0=makeQuery(id+"F4.imprint","IMPRINT",FACE,{"disambiguationData":[TD([[makeQuery(id+"F4.imprint","IMPRINT",EDGE,{"derivedFrom":subQ4}),-1.0]])]});}
            var Q1;
            Q1=makeQuery(id+"F4.imprint","IMPRINT",FACE,{"disambiguationData":[TD([[makeQuery(id+"F4.imprint","IMPRINT",EDGE,{"derivedFrom":sQuery(id+"F4.wireOp",EDGE,"E338")}),-1.0]])]});
            var Q2;
            Q2=makeQuery(id+"F4.imprint","IMPRINT",FACE,{"disambiguationData":[TD([[makeQuery(id+"F4.imprint","IMPRINT",EDGE,{"derivedFrom":sQuery(id+"F4.wireOp",EDGE,"E356")}),1.0]])]});
            var Q3;
            Q3=makeQuery(id+"F4.imprint","IMPRINT",FACE,{"disambiguationData":[TD([[makeQuery(id+"F4.imprint","IMPRINT",EDGE,{"derivedFrom":sQuery(id+"F4.wireOp",EDGE,"E377")}),-1.0]])]});
            var Q4;
            Q4=makeQuery(id+"F4.imprint","IMPRINT",FACE,{"disambiguationData":[TD([[makeQuery(id+"F4.imprint","IMPRINT",EDGE,{"derivedFrom":sQuery(id+"F4.wireOp",EDGE,"E374")}),1.0]])]});
            var Q5;
            Q5=makeQuery(id+"F4.imprint","IMPRINT",FACE,{"disambiguationData":[TD([[makeQuery(id+"F4.imprint","IMPRINT",EDGE,{"derivedFrom":sQuery(id+"F4.wireOp",EDGE,"E289")}),1.0]])]});
            var Q6;
            Q6=makeQuery(id+"F4.imprint","IMPRINT",FACE,{"disambiguationData":[TD([[makeQuery(id+"F4.imprint","IMPRINT",EDGE,{"derivedFrom":sQuery(id+"F4.wireOp",EDGE,"E259")}),1.0]])]});
            extrude(context, id + "F5", {"entities" : qUnion([Q0, Q1, Q2, Q3, Q4, Q5, Q6]), "operationType" : NewBodyOperationType.REMOVE, "oppositeDirection" : true, "depth" : 1 * mm, "offsetDistance" : 25 * mm});
        }
        {
            var Q0;
            {var subQ120=sQuery(id+"F1.wireOp",EDGE,"E68");var subQ122=sQuery(id+"F1.wireOp",EDGE,"E66");var subQ124=sQuery(id+"F1.wireOp",EDGE,"E65");var subQ126=sQuery(id+"F1.wireOp",EDGE,"E64");var subQ128=sQuery(id+"F1.wireOp",EDGE,"E63");var subQ132=sQuery(id+"F1.wireOp",EDGE,"E62");var subQ135=sQuery(id+"F1.wireOp",EDGE,"E61");var subQ138=sQuery(id+"F1.wireOp",EDGE,"E60");var subQ142=sQuery(id+"F1.wireOp",EDGE,"E59");var subQ145=sQuery(id+"F1.wireOp",EDGE,"E58");var subQ148=sQuery(id+"F1.wireOp",EDGE,"E57");var subQ151=sQuery(id+"F1.wireOp",EDGE,"E56");var subQ154=sQuery(id+"F1.wireOp",EDGE,"E55");var subQ157=sQuery(id+"F1.wireOp",EDGE,"E54");var subQ160=sQuery(id+"F1.wireOp",EDGE,"E53");var subQ163=sQuery(id+"F1.wireOp",EDGE,"E52");var subQ166=sQuery(id+"F1.wireOp",EDGE,"E51");var subQ169=sQuery(id+"F1.wireOp",EDGE,"E50");var subQ172=sQuery(id+"F1.wireOp",EDGE,"E49");var subQ175=sQuery(id+"F1.wireOp",EDGE,"E48");var subQ178=sQuery(id+"F1.wireOp",EDGE,"E47");var subQ181=sQuery(id+"F1.wireOp",EDGE,"E46");var subQ184=sQuery(id+"F1.wireOp",EDGE,"E45");var subQ187=sQuery(id+"F1.wireOp",EDGE,"E44");var subQ190=sQuery(id+"F1.wireOp",EDGE,"E43");var subQ191=sQuery(id+"F0.wireOp",EDGE,"E1");var subQ195=sQuery(id+"F1.wireOp",EDGE,"E42");var subQ198=sQuery(id+"F1.wireOp",EDGE,"E41");var subQ199=sQuery(id+"F1.wireOp",EDGE,"E40");var subQ200=sQuery(id+"F0.wireOp",EDGE,"E0");var subQ201=makeQuery(id+"F2.opExtrude","SWEPT_FACE",FACE,{"disambiguationData":[OSD([subQ200])]});var subQ204=sQuery(id+"F1.wireOp",EDGE,"E39");var subQ207=sQuery(id+"F1.wireOp",EDGE,"E38");var subQ210=sQuery(id+"F1.wireOp",EDGE,"E37");var subQ213=sQuery(id+"F1.wireOp",EDGE,"E36");var subQ216=sQuery(id+"F1.wireOp",EDGE,"E35");var subQ219=sQuery(id+"F1.wireOp",EDGE,"E34");var subQ222=sQuery(id+"F1.wireOp",EDGE,"E33");var subQ225=sQuery(id+"F1.wireOp",EDGE,"E32");var subQ228=sQuery(id+"F1.wireOp",EDGE,"E31");var subQ231=sQuery(id+"F1.wireOp",EDGE,"E30");var subQ234=sQuery(id+"F1.wireOp",EDGE,"E29");var subQ237=sQuery(id+"F1.wireOp",EDGE,"E28");var subQ240=sQuery(id+"F1.wireOp",EDGE,"E27");var subQ243=sQuery(id+"F1.wireOp",EDGE,"E26");var subQ246=sQuery(id+"F1.wireOp",EDGE,"E25");var subQ249=sQuery(id+"F1.wireOp",EDGE,"E24");var subQ252=sQuery(id+"F1.wireOp",EDGE,"E23");var subQ255=sQuery(id+"F1.wireOp",EDGE,"E22");var subQ258=sQuery(id+"F1.wireOp",EDGE,"E21");var subQ261=sQuery(id+"F1.wireOp",EDGE,"E20");var subQ264=sQuery(id+"F1.wireOp",EDGE,"E19");var subQ267=sQuery(id+"F1.wireOp",EDGE,"E18");var subQ270=sQuery(id+"F1.wireOp",EDGE,"E17");var subQ273=sQuery(id+"F1.wireOp",EDGE,"E16");var subQ276=sQuery(id+"F1.wireOp",EDGE,"E15");var subQ279=sQuery(id+"F1.wireOp",EDGE,"E14");var subQ282=sQuery(id+"F1.wireOp",EDGE,"E13");var subQ285=sQuery(id+"F1.wireOp",EDGE,"E12");var subQ288=sQuery(id+"F1.wireOp",EDGE,"E11");var subQ291=sQuery(id+"F1.wireOp",EDGE,"E10");var subQ294=sQuery(id+"F1.wireOp",EDGE,"E9");var subQ297=sQuery(id+"F1.wireOp",EDGE,"E7");var subQ1208=sQuery(id+"F1.wireOp",EDGE,"E67");var subQ1209=sQuery(id+"F1.wireOp",EDGE,"E8");var subQ1210=sQuery(id+"F1.wireOp",EDGE,"E6.0");Q0=makeQuery(id+"FciJOSwSTCKuNuW_1.2.F5.boolean.opBoolean","SPLIT",FACE,{"disambiguationData":[TD([subQ201])],"derivedFrom":makeQuery(id+"FciJOSwSTCKuNuW_1.2.F3.boolean.opBoolean","MERGE",FACE,{"derivedFrom":[makeQuery(id+"FciJOSwSTCKuNuW_1.1.F5.boolean.opBoolean","SPLIT",FACE,{"disambiguationData":[TD([subQ201])],"derivedFrom":makeQuery(id+"FciJOSwSTCKuNuW_1.1.F3.boolean.opBoolean","MERGE",FACE,{"derivedFrom":[makeQuery(id+"F5.boolean.opBoolean","SPLIT",FACE,{"disambiguationData":[TD([subQ201])],"derivedFrom":makeQuery(id+"F3.boolean.opBoolean","MERGE",FACE,{"derivedFrom":[makeQuery(id+"F2.opExtrude","CAP_FACE",FACE,{"disambiguationData":[OSD([subQ200,subQ191])],"isStart":false}),makeQuery(id+"F3.opExtrude","CAP_FACE",FACE,{"disambiguationData":[OSD([subQ1210,subQ297,subQ1209,subQ294,subQ291,subQ288,subQ285,subQ282,subQ279,subQ276,subQ273,subQ270,subQ267,subQ264,subQ261,subQ258,subQ255,subQ252,subQ249,subQ246,subQ243,subQ240,subQ237,subQ234,subQ231,subQ228,subQ225,subQ222,subQ219,subQ216,subQ213,subQ210,subQ207,subQ204,subQ199,subQ198,subQ195,subQ190,subQ187,subQ184,subQ181,subQ178,subQ175,subQ172,subQ169,subQ166,subQ163,subQ160,subQ157,subQ154,subQ151,subQ148,subQ145,subQ142,subQ138,subQ135,subQ132,subQ128,subQ126,subQ124,subQ122,subQ1208,subQ120])],"isStart":false})]})}),makeQuery(id+"FciJOSwSTCKuNuW_1.1.F3.opExtrude","CAP_FACE",FACE,{"disambiguationData":[OSD([subQ1210,subQ297,subQ1209,subQ294,subQ291,subQ288,subQ285,subQ282,subQ279,subQ276,subQ273,subQ270,subQ267,subQ264,subQ261,subQ258,subQ255,subQ252,subQ249,subQ246,subQ243,subQ240,subQ237,subQ234,subQ231,subQ228,subQ225,subQ222,subQ219,subQ216,subQ213,subQ210,subQ207,subQ204,subQ199,subQ198,subQ195,subQ190,subQ187,subQ184,subQ181,subQ178,subQ175,subQ172,subQ169,subQ166,subQ163,subQ160,subQ157,subQ154,subQ151,subQ148,subQ145,subQ142,subQ138,subQ135,subQ132,subQ128,subQ126,subQ124,subQ122,subQ1208,subQ120])],"isStart":false})]})}),makeQuery(id+"FciJOSwSTCKuNuW_1.2.F3.opExtrude","CAP_FACE",FACE,{"disambiguationData":[OSD([subQ1210,subQ297,subQ1209,subQ294,subQ291,subQ288,subQ285,subQ282,subQ279,subQ276,subQ273,subQ270,subQ267,subQ264,subQ261,subQ258,subQ255,subQ252,subQ249,subQ246,subQ243,subQ240,subQ237,subQ234,subQ231,subQ228,subQ225,subQ222,subQ219,subQ216,subQ213,subQ210,subQ207,subQ204,subQ199,subQ198,subQ195,subQ190,subQ187,subQ184,subQ181,subQ178,subQ175,subQ172,subQ169,subQ166,subQ163,subQ160,subQ157,subQ154,subQ151,subQ148,subQ145,subQ142,subQ138,subQ135,subQ132,subQ128,subQ126,subQ124,subQ122,subQ1208,subQ120])],"isStart":false})]})});}
            var sketch = newSketch(context, id + "F6", { "sketchPlane" : qUnion([Q0])});
            skCircle(sketch, "E381", {"center": v(0.17, -13.44) * mm, "radius": 0.26 * mm});
            skCircle(sketch, "E382", {"center": v(-11.76, 6.57) * mm, "radius": 0.2 * mm});
            skCircle(sketch, "E383", {"center": v(11.56, 6.91) * mm, "radius": 0.2 * mm});
            skSolve(sketch);
        }
        {
            var Q0;
            Q0 = qSketchRegion(id + "F6", true);
            extrude(context, id + "F7", {"entities" : qUnion([Q0]), "operationType" : NewBodyOperationType.ADD, "oppositeDirection" : true, "depth" : 7 * mm, "offsetDistance" : 25 * mm});
        }
    });
